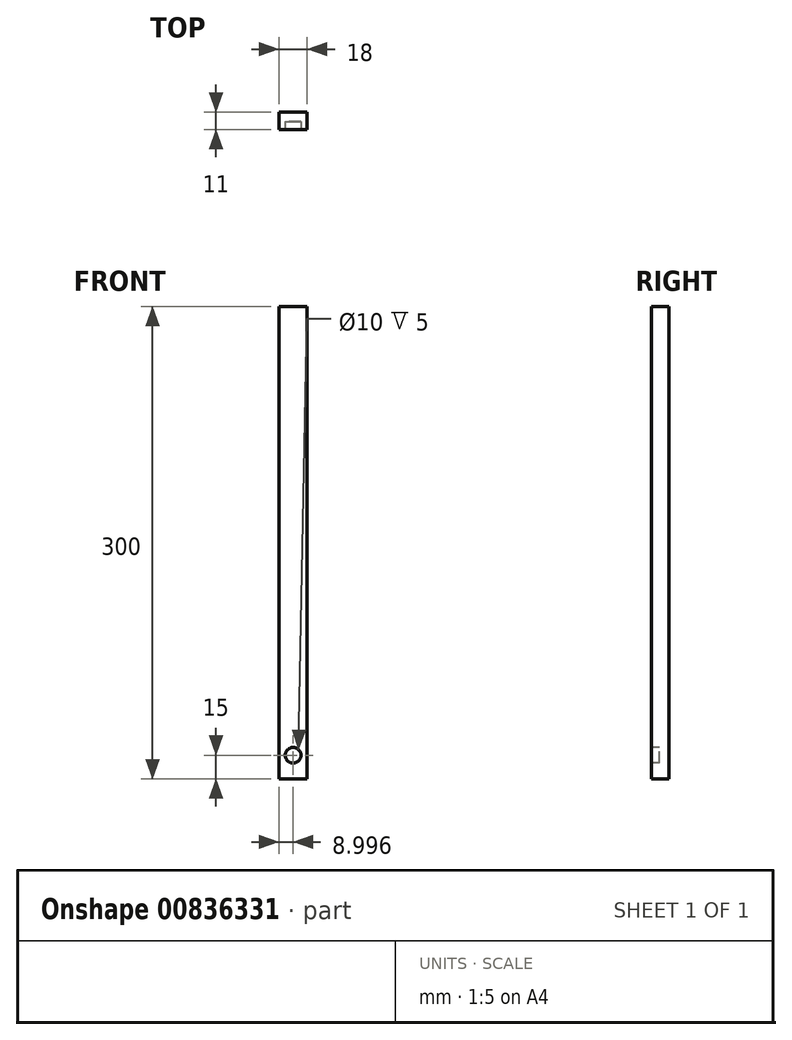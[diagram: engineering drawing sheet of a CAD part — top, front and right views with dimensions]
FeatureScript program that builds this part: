
annotation { "Feature Type Name" : "Feature", "Feature Type Description" : "" }
export const myFeature = defineFeature(function(context is Context, id is Id, definition is map)
    precondition{}
    {
        {
            var Q0;
            Q0=qCreatedBy(makeId("Top.planeOp"),FACE);
            var sketch = newSketch(context, id + "F0", { "sketchPlane" : qUnion([Q0])});
            skLineSegment(sketch, "E0.bottom", {"start": v(-3.28, -0.88) * mm, "end": v(14.72, -0.88) * mm});
            skLineSegment(sketch, "E0.top", {"start": v(-3.28, -11.88) * mm, "end": v(14.72, -11.88) * mm});
            skLineSegment(sketch, "E0.left", {"start": v(-3.28, -0.88) * mm, "end": v(-3.28, -11.88) * mm});
            skLineSegment(sketch, "E0.right", {"start": v(14.72, -0.88) * mm, "end": v(14.72, -11.88) * mm});
            skSolve(sketch);
        }
        {
            var Q0;
            Q0 = qSketchRegion(id + "F0", true);
            extrude(context, id + "F1", {"entities" : qUnion([Q0]), "depth" : 300 * mm, "offsetDistance" : 25 * mm});
        }
        {
            var Q0;
            Q0=makeQuery(id+"F1.opExtrude","SWEPT_FACE",FACE,{"disambiguationData":[OSD([sQuery(id+"F0.wireOp",EDGE,"E0.top")])]});
            var sketch = newSketch(context, id + "F2", { "sketchPlane" : qUnion([Q0])});
            skCircle(sketch, "E1", {"center": v(5.72, 15) * mm, "radius": 5 * mm});
            skSolve(sketch);
        }
        {
            var Q0;
            Q0=makeQuery(id+"F2.imprint","IMPRINT",FACE,{"disambiguationData":[TD([[makeQuery(id+"F2.imprint","IMPRINT",EDGE,{"derivedFrom":sQuery(id+"F2.wireOp",EDGE,"E1")}),1.0]])]});
            extrude(context, id + "F3", {"entities" : qUnion([Q0]), "operationType" : NewBodyOperationType.REMOVE, "oppositeDirection" : true, "depth" : 5 * mm, "offsetDistance" : 25 * mm});
        }
    });
